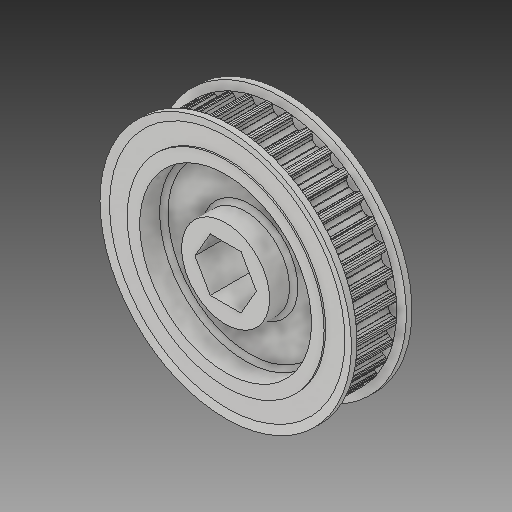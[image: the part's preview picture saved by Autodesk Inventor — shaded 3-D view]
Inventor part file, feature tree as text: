
AUTODESK INVENTOR PART (.ipt)
format: ipt  version: 2017 (Build 210142000, 142)  size: 843,776 bytes
history: native  units: in
note: dims shown in document units (in); Inventor stores cm internally (conversion verified against a paired STEP export)
features: mirror x1
ambient origin geometry x8: Origin, YZ Plane, XZ Plane, XY Plane, X Axis, Y Axis, Z Axis, Center Point
bodies: Solid1 (feature_tree)
feature tree (1):
  mirror  "Mirror1"
